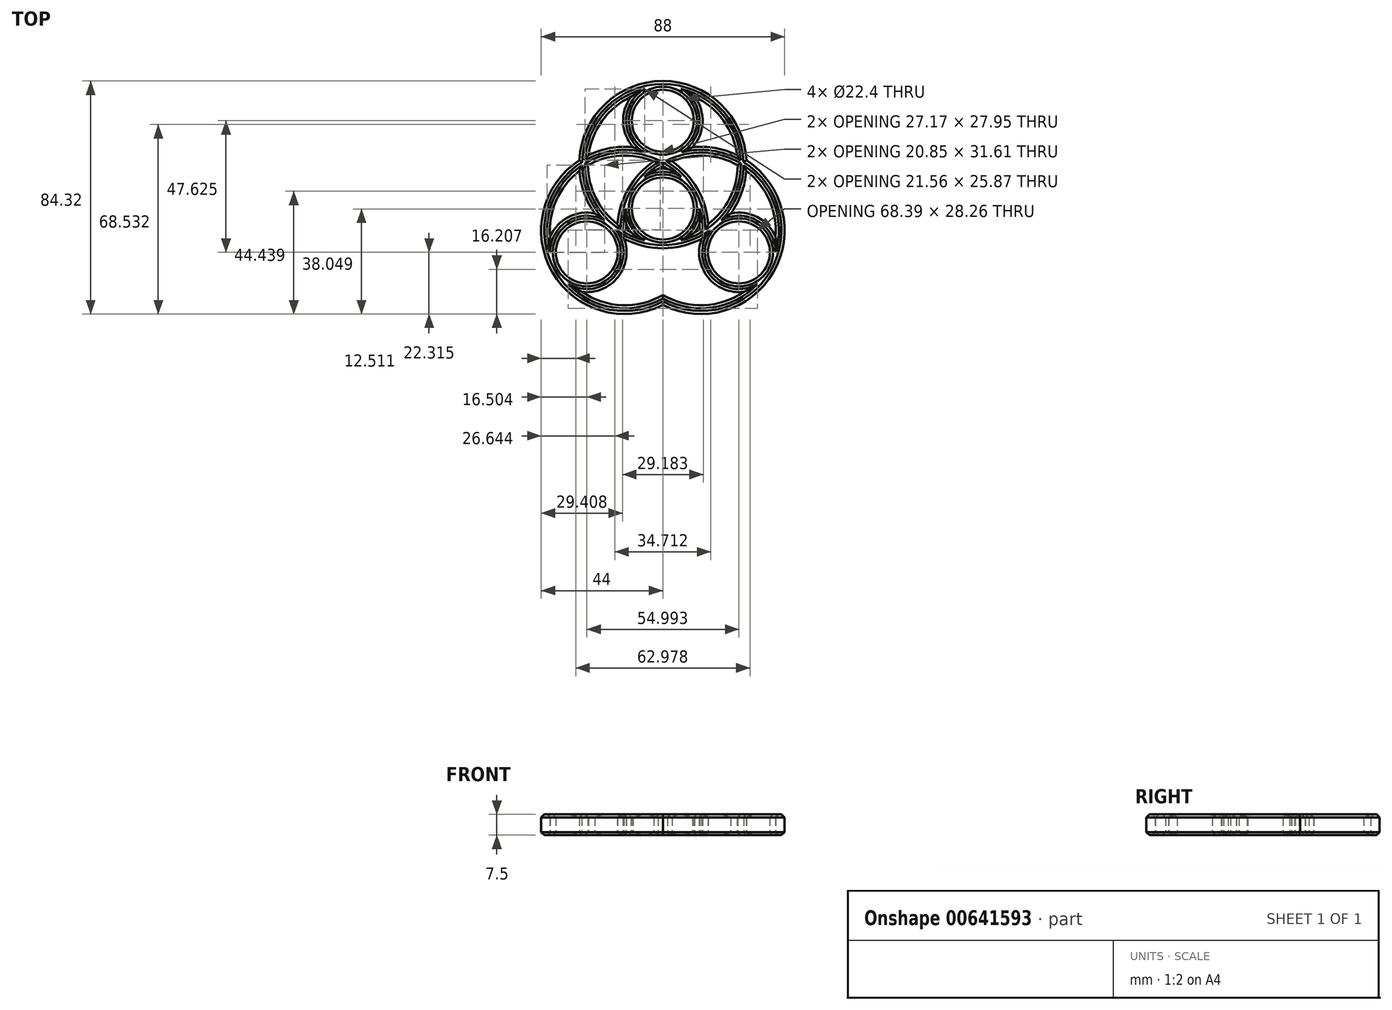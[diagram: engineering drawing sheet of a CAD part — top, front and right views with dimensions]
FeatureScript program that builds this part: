
annotation { "Feature Type Name" : "Feature", "Feature Type Description" : "" }
export const myFeature = defineFeature(function(context is Context, id is Id, definition is map)
    precondition{}
    {
        {
            var Q0;
            Q0=qCreatedBy(makeId("Top.planeOp"),FACE);
            var sketch = newSketch(context, id + "F0", { "sketchPlane" : qUnion([Q0])});
            skCircle(sketch, "E0", {"center": v(0, 0) * mm, "radius": 11.2 * mm});
            skCircle(sketch, "E1", {"center": v(0, 31.75) * mm, "radius": 11.2 * mm});
            skCircle(sketch, "E2", {"center": v(0, 31.75) * mm, "radius": 14.38 * mm});
            skCircle(sketch, "E3", {"center": v(0, 0) * mm, "radius": 14.38 * mm});
            skCircle(sketch, "E4", {"center": v(0, 15.88) * mm, "radius": 30.25 * mm});
            skCircle(sketch, "E5", {"center": v(0, 15.88) * mm, "radius": 27.08 * mm});
            skCircle(sketch, "E6.1.0", {"center": v(-27.5, -15.87) * mm, "radius": 11.2 * mm});
            skCircle(sketch, "E6.1.1", {"center": v(-27.5, -15.87) * mm, "radius": 14.38 * mm});
            skCircle(sketch, "E6.1.2", {"center": v(-13.75, -7.94) * mm, "radius": 27.08 * mm});
            skCircle(sketch, "E6.1.3", {"center": v(-13.75, -7.94) * mm, "radius": 30.25 * mm});
            skCircle(sketch, "E6.2.0", {"center": v(27.5, -15.88) * mm, "radius": 11.2 * mm});
            skCircle(sketch, "E6.2.1", {"center": v(27.5, -15.88) * mm, "radius": 14.38 * mm});
            skCircle(sketch, "E6.2.2", {"center": v(13.75, -7.94) * mm, "radius": 27.08 * mm});
            skCircle(sketch, "E6.2.3", {"center": v(13.75, -7.94) * mm, "radius": 30.25 * mm});
            skSolve(sketch);
        }
        {
            var Q0;
            Q0=qSketchRegion(id+"F0",true);
            var Q1;
            {var subQ0=sQuery(id+"F0.wireOp",EDGE,"E6.1.3");var subQ1=sQuery(id+"F0.wireOp",EDGE,"E1");var subQ2=makeQuery(id+"F0.imprint","INTERSECT",VERTEX,{"disambiguationData":[OD(0.0)],"derivedFrom":[subQ1,subQ0]});Q1=makeQuery(id+"F0.imprint","IMPRINT",FACE,{"disambiguationData":[TD([[makeQuery(id+"F0.imprint","IMPRINT",EDGE,{"disambiguationData":[TD([[subQ2,1.0]])],"derivedFrom":subQ1}),-1.0]])]});}
            var Q2;
            {var subQ0=sQuery(id+"F0.wireOp",EDGE,"E5");var subQ1=sQuery(id+"F0.wireOp",EDGE,"E1");var subQ2=makeQuery(id+"F0.imprint","INTERSECT",VERTEX,{"derivedFrom":[subQ1,subQ0]});Q2=makeQuery(id+"F0.imprint","IMPRINT",FACE,{"disambiguationData":[TD([[makeQuery(id+"F0.imprint","IMPRINT",EDGE,{"disambiguationData":[TD([[subQ2,1.0]])],"derivedFrom":subQ1}),-1.0]])]});}
            var Q3;
            {var subQ0=sQuery(id+"F0.wireOp",EDGE,"E6.1.1");var subQ1=sQuery(id+"F0.wireOp",EDGE,"E4");var subQ2=makeQuery(id+"F0.imprint","INTERSECT",VERTEX,{"disambiguationData":[OD(0.0)],"derivedFrom":[subQ1,subQ0]});Q3=makeQuery(id+"F0.imprint","IMPRINT",FACE,{"disambiguationData":[TD([[makeQuery(id+"F0.imprint","IMPRINT",EDGE,{"disambiguationData":[TD([[subQ2,-1.0]])],"derivedFrom":subQ1}),-1.0]])]});}
            var Q4;
            {var subQ0=sQuery(id+"F0.wireOp",EDGE,"E6.2.3");var subQ1=sQuery(id+"F0.wireOp",EDGE,"E6.1.0");var subQ2=makeQuery(id+"F0.imprint","INTERSECT",VERTEX,{"disambiguationData":[OD(0.0)],"derivedFrom":[subQ1,subQ0]});Q4=makeQuery(id+"F0.imprint","IMPRINT",FACE,{"disambiguationData":[TD([[makeQuery(id+"F0.imprint","IMPRINT",EDGE,{"disambiguationData":[TD([[subQ2,1.0]])],"derivedFrom":subQ1}),-1.0]])]});}
            var Q5;
            {var subQ0=sQuery(id+"F0.wireOp",EDGE,"E6.2.1");var subQ1=sQuery(id+"F0.wireOp",EDGE,"E6.1.3");var subQ2=makeQuery(id+"F0.imprint","INTERSECT",VERTEX,{"disambiguationData":[OD(0.0)],"derivedFrom":[subQ1,subQ0]});Q5=makeQuery(id+"F0.imprint","IMPRINT",FACE,{"disambiguationData":[TD([[makeQuery(id+"F0.imprint","IMPRINT",EDGE,{"disambiguationData":[TD([[subQ2,-1.0]])],"derivedFrom":subQ1}),-1.0]])]});}
            var Q6;
            {var subQ0=sQuery(id+"F0.wireOp",EDGE,"E6.2.0");var subQ1=sQuery(id+"F0.wireOp",EDGE,"E4");var subQ2=makeQuery(id+"F0.imprint","INTERSECT",VERTEX,{"disambiguationData":[OD(1.0)],"derivedFrom":[subQ1,subQ0]});Q6=makeQuery(id+"F0.imprint","IMPRINT",FACE,{"disambiguationData":[TD([[makeQuery(id+"F0.imprint","IMPRINT",EDGE,{"disambiguationData":[TD([[subQ2,-1.0]])],"derivedFrom":subQ1}),-1.0]])]});}
            var Q7;
            {var subQ0=sQuery(id+"F0.wireOp",EDGE,"E6.2.2");var subQ1=sQuery(id+"F0.wireOp",EDGE,"E2");var subQ2=makeQuery(id+"F0.imprint","INTERSECT",VERTEX,{"disambiguationData":[OD(1.0)],"derivedFrom":[subQ1,subQ0]});Q7=makeQuery(id+"F0.imprint","IMPRINT",FACE,{"disambiguationData":[TD([[makeQuery(id+"F0.imprint","IMPRINT",EDGE,{"disambiguationData":[TD([[subQ2,-1.0]])],"derivedFrom":subQ1}),-1.0]])]});}
            var Q8;
            {var subQ3=sQuery(id+"F0.wireOp",EDGE,"E6.2.3");var subQ5=sQuery(id+"F0.wireOp",EDGE,"E1");var subQ6=makeQuery(id+"F0.imprint","INTERSECT",VERTEX,{"disambiguationData":[OD(0.0)],"derivedFrom":[subQ5,subQ3]});Q8=makeQuery(id+"F0.imprint","IMPRINT",FACE,{"disambiguationData":[TD([[makeQuery(id+"F0.imprint","IMPRINT",EDGE,{"disambiguationData":[TD([[subQ6,-1.0]])],"derivedFrom":subQ5}),-1.0]])]});}
            var Q9;
            {var subQ6=sQuery(id+"F0.wireOp",EDGE,"E6.1.3");var subQ8=sQuery(id+"F0.wireOp",EDGE,"E1");var subQ9=makeQuery(id+"F0.imprint","INTERSECT",VERTEX,{"disambiguationData":[OD(0.0)],"derivedFrom":[subQ8,subQ6]});Q9=makeQuery(id+"F0.imprint","IMPRINT",FACE,{"disambiguationData":[TD([[makeQuery(id+"F0.imprint","IMPRINT",EDGE,{"disambiguationData":[TD([[subQ9,-1.0]])],"derivedFrom":subQ8}),-1.0]])]});}
            var Q10;
            {var subQ0=sQuery(id+"F0.wireOp",EDGE,"E6.1.3");var subQ1=sQuery(id+"F0.wireOp",EDGE,"E2");var subQ2=makeQuery(id+"F0.imprint","INTERSECT",VERTEX,{"disambiguationData":[OD(0.0)],"derivedFrom":[subQ1,subQ0]});Q10=makeQuery(id+"F0.imprint","IMPRINT",FACE,{"disambiguationData":[TD([[makeQuery(id+"F0.imprint","IMPRINT",EDGE,{"disambiguationData":[TD([[subQ2,-1.0]])],"derivedFrom":subQ1}),-1.0]])]});}
            var Q11;
            {var subQ0=sQuery(id+"F0.wireOp",EDGE,"E6.1.3");var subQ1=sQuery(id+"F0.wireOp",EDGE,"E1");var subQ2=makeQuery(id+"F0.imprint","INTERSECT",VERTEX,{"disambiguationData":[OD(1.0)],"derivedFrom":[subQ1,subQ0]});Q11=makeQuery(id+"F0.imprint","IMPRINT",FACE,{"disambiguationData":[TD([[makeQuery(id+"F0.imprint","IMPRINT",EDGE,{"disambiguationData":[TD([[subQ2,-1.0]])],"derivedFrom":subQ1}),-1.0]])]});}
            var Q12;
            {var subQ0=sQuery(id+"F0.wireOp",EDGE,"E6.2.3");var subQ1=sQuery(id+"F0.wireOp",EDGE,"E2");var subQ2=makeQuery(id+"F0.imprint","INTERSECT",VERTEX,{"disambiguationData":[OD(0.0)],"derivedFrom":[subQ1,subQ0]});Q12=makeQuery(id+"F0.imprint","IMPRINT",FACE,{"disambiguationData":[TD([[makeQuery(id+"F0.imprint","IMPRINT",EDGE,{"disambiguationData":[TD([[subQ2,-1.0]])],"derivedFrom":subQ1}),1.0]])]});}
            var Q13;
            {var subQ1=sQuery(id+"F0.wireOp",EDGE,"E4");var subQ6=sQuery(id+"F0.wireOp",EDGE,"E6.1.1");var subQ7=makeQuery(id+"F0.imprint","INTERSECT",VERTEX,{"disambiguationData":[OD(0.0)],"derivedFrom":[subQ1,subQ6]});Q13=makeQuery(id+"F0.imprint","IMPRINT",FACE,{"disambiguationData":[TD([[makeQuery(id+"F0.imprint","IMPRINT",EDGE,{"disambiguationData":[TD([[subQ7,-1.0]])],"derivedFrom":subQ1}),1.0]])]});}
            var Q14;
            {var subQ1=sQuery(id+"F0.wireOp",EDGE,"E4");var subQ5=sQuery(id+"F0.wireOp",EDGE,"E6.2.3");var subQ11=makeQuery(id+"F0.imprint","INTERSECT",VERTEX,{"disambiguationData":[OD(1.0)],"derivedFrom":[subQ1,subQ5]});Q14=makeQuery(id+"F0.imprint","IMPRINT",FACE,{"disambiguationData":[TD([[makeQuery(id+"F0.imprint","IMPRINT",EDGE,{"disambiguationData":[TD([[subQ11,-1.0]])],"derivedFrom":subQ1}),-1.0]])]});}
            var Q15;
            {var subQ0=sQuery(id+"F0.wireOp",EDGE,"E6.1.0");var subQ1=sQuery(id+"F0.wireOp",EDGE,"E4");var subQ2=makeQuery(id+"F0.imprint","INTERSECT",VERTEX,{"disambiguationData":[OD(1.0)],"derivedFrom":[subQ1,subQ0]});Q15=makeQuery(id+"F0.imprint","IMPRINT",FACE,{"disambiguationData":[TD([[makeQuery(id+"F0.imprint","IMPRINT",EDGE,{"disambiguationData":[TD([[subQ2,-1.0]])],"derivedFrom":subQ1}),-1.0]])]});}
            var Q16;
            {var subQ0=sQuery(id+"F0.wireOp",EDGE,"E6.2.3");var subQ1=sQuery(id+"F0.wireOp",EDGE,"E4");var subQ2=makeQuery(id+"F0.imprint","INTERSECT",VERTEX,{"disambiguationData":[OD(1.0)],"derivedFrom":[subQ1,subQ0]});Q16=makeQuery(id+"F0.imprint","IMPRINT",FACE,{"disambiguationData":[TD([[makeQuery(id+"F0.imprint","IMPRINT",EDGE,{"disambiguationData":[TD([[subQ2,-1.0]])],"derivedFrom":subQ1}),1.0]])]});}
            var Q17;
            {var subQ0=sQuery(id+"F0.wireOp",EDGE,"E6.1.2");var subQ1=sQuery(id+"F0.wireOp",EDGE,"E4");var subQ2=makeQuery(id+"F0.imprint","INTERSECT",VERTEX,{"disambiguationData":[OD(0.0)],"derivedFrom":[subQ1,subQ0]});Q17=makeQuery(id+"F0.imprint","IMPRINT",FACE,{"disambiguationData":[TD([[makeQuery(id+"F0.imprint","IMPRINT",EDGE,{"disambiguationData":[TD([[subQ2,-1.0]])],"derivedFrom":subQ1}),1.0]])]});}
            var Q18;
            {var subQ0=sQuery(id+"F0.wireOp",EDGE,"E6.2.3");var subQ1=sQuery(id+"F0.wireOp",EDGE,"E6.1.1");var subQ2=makeQuery(id+"F0.imprint","INTERSECT",VERTEX,{"disambiguationData":[OD(0.0)],"derivedFrom":[subQ1,subQ0]});Q18=makeQuery(id+"F0.imprint","IMPRINT",FACE,{"disambiguationData":[TD([[makeQuery(id+"F0.imprint","IMPRINT",EDGE,{"disambiguationData":[TD([[subQ2,-1.0]])],"derivedFrom":subQ1}),-1.0]])]});}
            var Q19;
            {var subQ0=sQuery(id+"F0.wireOp",EDGE,"E6.2.2");var subQ1=sQuery(id+"F0.wireOp",EDGE,"E6.1.2");var subQ2=makeQuery(id+"F0.imprint","INTERSECT",VERTEX,{"disambiguationData":[OD(0.0)],"derivedFrom":[subQ1,subQ0]});Q19=makeQuery(id+"F0.imprint","IMPRINT",FACE,{"disambiguationData":[TD([[makeQuery(id+"F0.imprint","IMPRINT",EDGE,{"disambiguationData":[TD([[subQ2,-1.0]])],"derivedFrom":subQ1}),-1.0]])]});}
            var Q20;
            {var subQ1=sQuery(id+"F0.wireOp",EDGE,"E4");var subQ5=sQuery(id+"F0.wireOp",EDGE,"E6.2.1");var subQ11=makeQuery(id+"F0.imprint","INTERSECT",VERTEX,{"disambiguationData":[OD(0.0)],"derivedFrom":[subQ1,subQ5]});Q20=makeQuery(id+"F0.imprint","IMPRINT",FACE,{"disambiguationData":[TD([[makeQuery(id+"F0.imprint","IMPRINT",EDGE,{"disambiguationData":[TD([[subQ11,-1.0]])],"derivedFrom":subQ1}),-1.0]])]});}
            var Q21;
            {var subQ0=sQuery(id+"F0.wireOp",EDGE,"E6.2.1");var subQ1=sQuery(id+"F0.wireOp",EDGE,"E4");var subQ2=makeQuery(id+"F0.imprint","INTERSECT",VERTEX,{"disambiguationData":[OD(0.0)],"derivedFrom":[subQ1,subQ0]});Q21=makeQuery(id+"F0.imprint","IMPRINT",FACE,{"disambiguationData":[TD([[makeQuery(id+"F0.imprint","IMPRINT",EDGE,{"disambiguationData":[TD([[subQ2,-1.0]])],"derivedFrom":subQ1}),1.0]])]});}
            var Q22;
            {var subQ0=sQuery(id+"F0.wireOp",EDGE,"E6.1.3");var subQ1=sQuery(id+"F0.wireOp",EDGE,"E4");var subQ2=makeQuery(id+"F0.imprint","INTERSECT",VERTEX,{"disambiguationData":[OD(1.0)],"derivedFrom":[subQ1,subQ0]});Q22=makeQuery(id+"F0.imprint","IMPRINT",FACE,{"disambiguationData":[TD([[makeQuery(id+"F0.imprint","IMPRINT",EDGE,{"disambiguationData":[TD([[subQ2,-1.0]])],"derivedFrom":subQ1}),1.0]])]});}
            var Q23;
            {var subQ0=sQuery(id+"F0.wireOp",EDGE,"E6.1.3");var subQ1=sQuery(id+"F0.wireOp",EDGE,"E4");var subQ2=makeQuery(id+"F0.imprint","INTERSECT",VERTEX,{"disambiguationData":[OD(1.0)],"derivedFrom":[subQ1,subQ0]});Q23=makeQuery(id+"F0.imprint","IMPRINT",FACE,{"disambiguationData":[TD([[makeQuery(id+"F0.imprint","IMPRINT",EDGE,{"disambiguationData":[TD([[subQ2,-1.0]])],"derivedFrom":subQ1}),-1.0]])]});}
            var Q24;
            {var subQ0=sQuery(id+"F0.wireOp",EDGE,"E6.2.1");var subQ1=sQuery(id+"F0.wireOp",EDGE,"E4");var subQ2=makeQuery(id+"F0.imprint","INTERSECT",VERTEX,{"disambiguationData":[OD(1.0)],"derivedFrom":[subQ1,subQ0]});Q24=makeQuery(id+"F0.imprint","IMPRINT",FACE,{"disambiguationData":[TD([[makeQuery(id+"F0.imprint","IMPRINT",EDGE,{"disambiguationData":[TD([[subQ2,-1.0]])],"derivedFrom":subQ1}),1.0]])]});}
            var Q25;
            {var subQ0=sQuery(id+"F0.wireOp",EDGE,"E6.2.2");var subQ1=sQuery(id+"F0.wireOp",EDGE,"E3");var subQ2=makeQuery(id+"F0.imprint","INTERSECT",VERTEX,{"disambiguationData":[OD(0.0)],"derivedFrom":[subQ1,subQ0]});Q25=makeQuery(id+"F0.imprint","IMPRINT",FACE,{"disambiguationData":[TD([[makeQuery(id+"F0.imprint","IMPRINT",EDGE,{"disambiguationData":[TD([[subQ2,-1.0]])],"derivedFrom":subQ1}),1.0]])]});}
            var Q26;
            {var subQ0=sQuery(id+"F0.wireOp",EDGE,"E6.2.2");var subQ1=sQuery(id+"F0.wireOp",EDGE,"E0");var subQ2=makeQuery(id+"F0.imprint","INTERSECT",VERTEX,{"derivedFrom":[subQ1,subQ0]});Q26=makeQuery(id+"F0.imprint","IMPRINT",FACE,{"disambiguationData":[TD([[makeQuery(id+"F0.imprint","IMPRINT",EDGE,{"disambiguationData":[TD([[subQ2,-1.0]])],"derivedFrom":subQ1}),-1.0]])]});}
            var Q27;
            {var subQ0=sQuery(id+"F0.wireOp",EDGE,"E5");var subQ1=sQuery(id+"F0.wireOp",EDGE,"E3");var subQ2=makeQuery(id+"F0.imprint","INTERSECT",VERTEX,{"disambiguationData":[OD(0.0)],"derivedFrom":[subQ1,subQ0]});Q27=makeQuery(id+"F0.imprint","IMPRINT",FACE,{"disambiguationData":[TD([[makeQuery(id+"F0.imprint","IMPRINT",EDGE,{"disambiguationData":[TD([[subQ2,-1.0]])],"derivedFrom":subQ1}),1.0]])]});}
            var Q28;
            {var subQ0=sQuery(id+"F0.wireOp",EDGE,"E6.1.2");var subQ1=sQuery(id+"F0.wireOp",EDGE,"E0");var subQ2=makeQuery(id+"F0.imprint","INTERSECT",VERTEX,{"derivedFrom":[subQ1,subQ0]});Q28=makeQuery(id+"F0.imprint","IMPRINT",FACE,{"disambiguationData":[TD([[makeQuery(id+"F0.imprint","IMPRINT",EDGE,{"disambiguationData":[TD([[subQ2,1.0]])],"derivedFrom":subQ1}),-1.0]])]});}
            var Q29;
            {var subQ0=sQuery(id+"F0.wireOp",EDGE,"E6.1.2");var subQ1=sQuery(id+"F0.wireOp",EDGE,"E3");var subQ2=makeQuery(id+"F0.imprint","INTERSECT",VERTEX,{"disambiguationData":[OD(0.0)],"derivedFrom":[subQ1,subQ0]});Q29=makeQuery(id+"F0.imprint","IMPRINT",FACE,{"disambiguationData":[TD([[makeQuery(id+"F0.imprint","IMPRINT",EDGE,{"disambiguationData":[TD([[subQ2,1.0]])],"derivedFrom":subQ1}),1.0]])]});}
            var Q30;
            {var subQ0=sQuery(id+"F0.wireOp",EDGE,"E6.1.2");var subQ1=sQuery(id+"F0.wireOp",EDGE,"E3");var subQ2=makeQuery(id+"F0.imprint","INTERSECT",VERTEX,{"disambiguationData":[OD(0.0)],"derivedFrom":[subQ1,subQ0]});Q30=makeQuery(id+"F0.imprint","IMPRINT",FACE,{"disambiguationData":[TD([[makeQuery(id+"F0.imprint","IMPRINT",EDGE,{"disambiguationData":[TD([[subQ2,1.0]])],"derivedFrom":subQ1}),-1.0]])]});}
            var Q31;
            {var subQ5=sQuery(id+"F0.wireOp",EDGE,"E6.2.3");var subQ7=sQuery(id+"F0.wireOp",EDGE,"E2");var subQ9=makeQuery(id+"F0.imprint","INTERSECT",VERTEX,{"disambiguationData":[OD(0.0)],"derivedFrom":[subQ7,subQ5]});Q31=makeQuery(id+"F0.imprint","IMPRINT",FACE,{"disambiguationData":[TD([[makeQuery(id+"F0.imprint","IMPRINT",EDGE,{"disambiguationData":[TD([[subQ9,-1.0]])],"derivedFrom":subQ7}),-1.0]])]});}
            var Q32;
            {var subQ0=sQuery(id+"F0.wireOp",EDGE,"E6.2.2");var subQ1=sQuery(id+"F0.wireOp",EDGE,"E3");var subQ2=makeQuery(id+"F0.imprint","INTERSECT",VERTEX,{"disambiguationData":[OD(0.0)],"derivedFrom":[subQ1,subQ0]});Q32=makeQuery(id+"F0.imprint","IMPRINT",FACE,{"disambiguationData":[TD([[makeQuery(id+"F0.imprint","IMPRINT",EDGE,{"disambiguationData":[TD([[subQ2,-1.0]])],"derivedFrom":subQ1}),-1.0]])]});}
            var Q33;
            {var subQ0=sQuery(id+"F0.wireOp",EDGE,"E6.2.3");var subQ1=sQuery(id+"F0.wireOp",EDGE,"E3");var subQ2=makeQuery(id+"F0.imprint","INTERSECT",VERTEX,{"derivedFrom":[subQ1,subQ0]});Q33=makeQuery(id+"F0.imprint","IMPRINT",FACE,{"disambiguationData":[TD([[makeQuery(id+"F0.imprint","IMPRINT",EDGE,{"disambiguationData":[TD([[subQ2,-1.0]])],"derivedFrom":subQ1}),-1.0]])]});}
            var Q34;
            {var subQ1=sQuery(id+"F0.wireOp",EDGE,"E4");var subQ5=sQuery(id+"F0.wireOp",EDGE,"E6.1.1");var subQ6=makeQuery(id+"F0.imprint","INTERSECT",VERTEX,{"disambiguationData":[OD(1.0)],"derivedFrom":[subQ1,subQ5]});Q34=makeQuery(id+"F0.imprint","IMPRINT",FACE,{"disambiguationData":[TD([[makeQuery(id+"F0.imprint","IMPRINT",EDGE,{"disambiguationData":[TD([[subQ6,-1.0]])],"derivedFrom":subQ1}),1.0]])]});}
            var Q35;
            {var subQ0=sQuery(id+"F0.wireOp",EDGE,"E5");var subQ1=sQuery(id+"F0.wireOp",EDGE,"E3");var subQ2=makeQuery(id+"F0.imprint","INTERSECT",VERTEX,{"disambiguationData":[OD(0.0)],"derivedFrom":[subQ1,subQ0]});Q35=makeQuery(id+"F0.imprint","IMPRINT",FACE,{"disambiguationData":[TD([[makeQuery(id+"F0.imprint","IMPRINT",EDGE,{"disambiguationData":[TD([[subQ2,-1.0]])],"derivedFrom":subQ1}),-1.0]])]});}
            var Q36;
            {var subQ0=sQuery(id+"F0.wireOp",EDGE,"E4");var subQ1=sQuery(id+"F0.wireOp",EDGE,"E3");var subQ2=makeQuery(id+"F0.imprint","INTERSECT",VERTEX,{"derivedFrom":[subQ1,subQ0]});Q36=makeQuery(id+"F0.imprint","IMPRINT",FACE,{"disambiguationData":[TD([[makeQuery(id+"F0.imprint","IMPRINT",EDGE,{"disambiguationData":[TD([[subQ2,-1.0]])],"derivedFrom":subQ1}),-1.0]])]});}
            var Q37;
            {var subQ5=sQuery(id+"F0.wireOp",EDGE,"E6.1.2");var subQ6=sQuery(id+"F0.wireOp",EDGE,"E4");var subQ7=makeQuery(id+"F0.imprint","INTERSECT",VERTEX,{"disambiguationData":[OD(1.0)],"derivedFrom":[subQ6,subQ5]});Q37=makeQuery(id+"F0.imprint","IMPRINT",FACE,{"disambiguationData":[TD([[makeQuery(id+"F0.imprint","IMPRINT",EDGE,{"disambiguationData":[TD([[subQ7,-1.0]])],"derivedFrom":subQ6}),1.0]])]});}
            var Q38;
            {var subQ0=sQuery(id+"F0.wireOp",EDGE,"E6.1.3");var subQ1=sQuery(id+"F0.wireOp",EDGE,"E3");var subQ2=makeQuery(id+"F0.imprint","INTERSECT",VERTEX,{"derivedFrom":[subQ1,subQ0]});Q38=makeQuery(id+"F0.imprint","IMPRINT",FACE,{"disambiguationData":[TD([[makeQuery(id+"F0.imprint","IMPRINT",EDGE,{"disambiguationData":[TD([[subQ2,1.0]])],"derivedFrom":subQ1}),-1.0]])]});}
            var Q39;
            {var subQ3=sQuery(id+"F0.wireOp",EDGE,"E6.1.3");var subQ5=sQuery(id+"F0.wireOp",EDGE,"E2");var subQ6=makeQuery(id+"F0.imprint","INTERSECT",VERTEX,{"disambiguationData":[OD(1.0)],"derivedFrom":[subQ5,subQ3]});Q39=makeQuery(id+"F0.imprint","IMPRINT",FACE,{"disambiguationData":[TD([[makeQuery(id+"F0.imprint","IMPRINT",EDGE,{"disambiguationData":[TD([[subQ6,-1.0]])],"derivedFrom":subQ5}),-1.0]])]});}
            var Q40;
            {var subQ0=sQuery(id+"F0.wireOp",EDGE,"E6.2.2");var subQ1=sQuery(id+"F0.wireOp",EDGE,"E0");var subQ2=makeQuery(id+"F0.imprint","INTERSECT",VERTEX,{"derivedFrom":[subQ1,subQ0]});Q40=makeQuery(id+"F0.imprint","IMPRINT",FACE,{"disambiguationData":[TD([[makeQuery(id+"F0.imprint","IMPRINT",EDGE,{"disambiguationData":[TD([[subQ2,1.0]])],"derivedFrom":subQ1}),-1.0]])]});}
            var Q41;
            {var subQ0=sQuery(id+"F0.wireOp",EDGE,"E6.1.3");var subQ1=sQuery(id+"F0.wireOp",EDGE,"E2");var subQ2=makeQuery(id+"F0.imprint","INTERSECT",VERTEX,{"disambiguationData":[OD(1.0)],"derivedFrom":[subQ1,subQ0]});Q41=makeQuery(id+"F0.imprint","IMPRINT",FACE,{"disambiguationData":[TD([[makeQuery(id+"F0.imprint","IMPRINT",EDGE,{"disambiguationData":[TD([[subQ2,-1.0]])],"derivedFrom":subQ1}),1.0]])]});}
            var Q42;
            {var subQ0=sQuery(id+"F0.wireOp",EDGE,"E6.1.3");var subQ1=sQuery(id+"F0.wireOp",EDGE,"E2");var subQ2=makeQuery(id+"F0.imprint","INTERSECT",VERTEX,{"disambiguationData":[OD(0.0)],"derivedFrom":[subQ1,subQ0]});Q42=makeQuery(id+"F0.imprint","IMPRINT",FACE,{"disambiguationData":[TD([[makeQuery(id+"F0.imprint","IMPRINT",EDGE,{"disambiguationData":[TD([[subQ2,-1.0]])],"derivedFrom":subQ1}),1.0]])]});}
            extrude(context, id + "F1", {"entities" : qUnion([Q0, Q1, Q2, Q3, Q4, Q5, Q6, Q7, Q8, Q9, Q10, Q11, Q12, Q13, Q14, Q15, Q16, Q17, Q18, Q19, Q20, Q21, Q22, Q23, Q24, Q25, Q26, Q27, Q28, Q29, Q30, Q31, Q32, Q33, Q34, Q35, Q36, Q37, Q38, Q39, Q40, Q41, Q42]), "depth" : 7.5 * mm, "offsetDistance" : 25.4 * mm});
        }
        {
            var Q0;
            Q0=makeQuery(id+"F1.opExtrude","CAP_FACE",FACE,{"disambiguationData":[OSD([sQuery(id+"F0.wireOp",EDGE,"E0"),sQuery(id+"F0.wireOp",EDGE,"E1"),sQuery(id+"F0.wireOp",EDGE,"E2"),sQuery(id+"F0.wireOp",EDGE,"E3"),sQuery(id+"F0.wireOp",EDGE,"E4"),sQuery(id+"F0.wireOp",EDGE,"E5"),sQuery(id+"F0.wireOp",EDGE,"E6.1.0"),sQuery(id+"F0.wireOp",EDGE,"E6.1.1"),sQuery(id+"F0.wireOp",EDGE,"E6.1.2"),sQuery(id+"F0.wireOp",EDGE,"E6.1.3"),sQuery(id+"F0.wireOp",EDGE,"E6.2.0"),sQuery(id+"F0.wireOp",EDGE,"E6.2.1"),sQuery(id+"F0.wireOp",EDGE,"E6.2.2"),sQuery(id+"F0.wireOp",EDGE,"E6.2.3")])],"isStart":false});
            var Q1;
            Q1=makeQuery(id+"F1.opExtrude","CAP_FACE",FACE,{"disambiguationData":[OSD([sQuery(id+"F0.wireOp",EDGE,"E0"),sQuery(id+"F0.wireOp",EDGE,"E1"),sQuery(id+"F0.wireOp",EDGE,"E2"),sQuery(id+"F0.wireOp",EDGE,"E3"),sQuery(id+"F0.wireOp",EDGE,"E4"),sQuery(id+"F0.wireOp",EDGE,"E5"),sQuery(id+"F0.wireOp",EDGE,"E6.1.0"),sQuery(id+"F0.wireOp",EDGE,"E6.1.1"),sQuery(id+"F0.wireOp",EDGE,"E6.1.2"),sQuery(id+"F0.wireOp",EDGE,"E6.1.3"),sQuery(id+"F0.wireOp",EDGE,"E6.2.0"),sQuery(id+"F0.wireOp",EDGE,"E6.2.1"),sQuery(id+"F0.wireOp",EDGE,"E6.2.2"),sQuery(id+"F0.wireOp",EDGE,"E6.2.3")])],"isStart":true});
            chamfer(context, id + "F2", {"entities" : qUnion([Q0, Q1]), "width" : 1.1 * mm, "tangentPropagation" : true});
        }
    });
